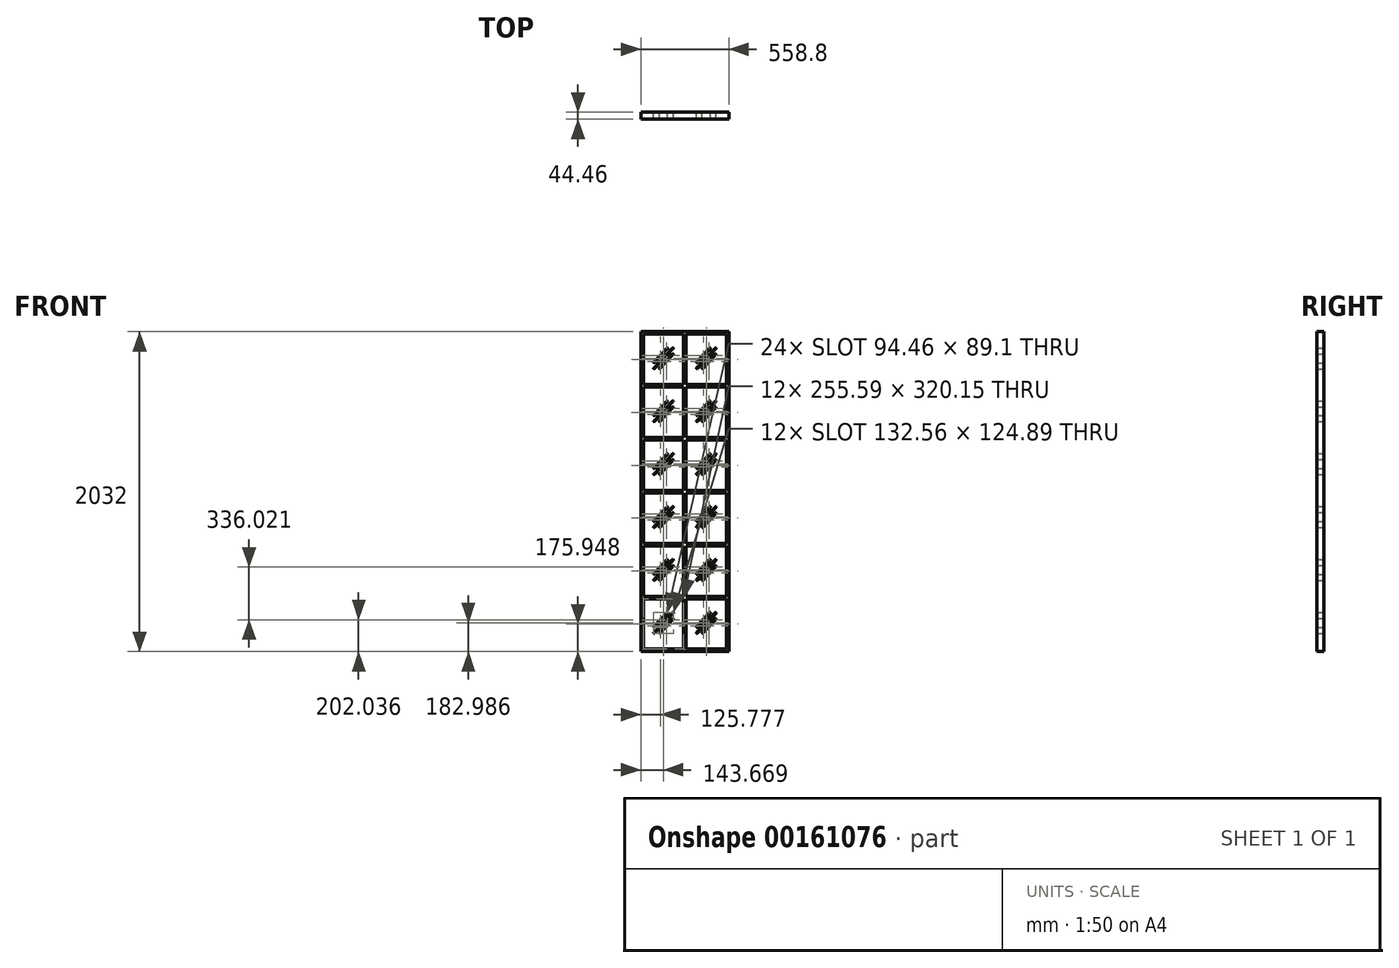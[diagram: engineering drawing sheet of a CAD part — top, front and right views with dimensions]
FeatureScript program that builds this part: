
annotation { "Feature Type Name" : "Feature", "Feature Type Description" : "" }
export const myFeature = defineFeature(function(context is Context, id is Id, definition is map)
    precondition{}
    {
        {
            var Q0;
            Q0=qCreatedBy(makeId("Front.planeOp"),FACE);
            var sketch = newSketch(context, id + "F0", { "sketchPlane" : qUnion([Q0])});
            skLineSegment(sketch, "E0.bottom", {"start": v(0, 0) * mm, "end": v(558.8, 0) * mm});
            skLineSegment(sketch, "E0.top", {"start": v(0, 2032) * mm, "end": v(558.8, 2032) * mm});
            skLineSegment(sketch, "E0.left", {"start": v(0, 0) * mm, "end": v(0, 2032) * mm});
            skLineSegment(sketch, "E0.right", {"start": v(558.8, 0) * mm, "end": v(558.8, 2032) * mm});
            skLineSegment(sketch, "E1.bottom", {"start": v(15.88, 15.88) * mm, "end": v(271.46, 15.88) * mm});
            skLineSegment(sketch, "E1.top", {"start": v(15.88, 336.02) * mm, "end": v(271.46, 336.02) * mm});
            skLineSegment(sketch, "E1.left", {"start": v(15.88, 15.88) * mm, "end": v(15.88, 336.02) * mm});
            skLineSegment(sketch, "E1.right", {"start": v(271.46, 15.88) * mm, "end": v(271.46, 336.02) * mm});
            skLineSegment(sketch, "E2.bottom", {"start": v(287.34, 15.88) * mm, "end": v(542.93, 15.88) * mm});
            skLineSegment(sketch, "E2.top", {"start": v(287.34, 336.02) * mm, "end": v(542.93, 336.02) * mm});
            skLineSegment(sketch, "E2.left", {"start": v(287.34, 15.88) * mm, "end": v(287.34, 336.02) * mm});
            skLineSegment(sketch, "E2.right", {"start": v(542.93, 15.88) * mm, "end": v(542.93, 336.02) * mm});
            skLineSegment(sketch, "E3.bottom", {"start": v(271.46, 351.9) * mm, "end": v(15.88, 351.9) * mm});
            skLineSegment(sketch, "E3.top", {"start": v(271.46, 672.04) * mm, "end": v(15.88, 672.04) * mm});
            skLineSegment(sketch, "E3.left", {"start": v(271.46, 351.9) * mm, "end": v(271.46, 672.04) * mm});
            skLineSegment(sketch, "E3.right", {"start": v(15.88, 351.9) * mm, "end": v(15.88, 672.04) * mm});
            skLineSegment(sketch, "E4.bottom", {"start": v(287.34, 351.9) * mm, "end": v(542.93, 351.9) * mm});
            skLineSegment(sketch, "E4.top", {"start": v(287.34, 672.04) * mm, "end": v(542.93, 672.04) * mm});
            skLineSegment(sketch, "E4.left", {"start": v(287.34, 351.9) * mm, "end": v(287.34, 672.04) * mm});
            skLineSegment(sketch, "E4.right", {"start": v(542.93, 351.9) * mm, "end": v(542.93, 672.04) * mm});
            skLineSegment(sketch, "E5.bottom", {"start": v(271.46, 687.92) * mm, "end": v(15.88, 687.92) * mm});
            skLineSegment(sketch, "E5.top", {"start": v(271.46, 1008.06) * mm, "end": v(15.88, 1008.06) * mm});
            skLineSegment(sketch, "E5.left", {"start": v(271.46, 687.92) * mm, "end": v(271.46, 1008.06) * mm});
            skLineSegment(sketch, "E5.right", {"start": v(15.88, 687.92) * mm, "end": v(15.87, 1008.06) * mm});
            skLineSegment(sketch, "E6.bottom", {"start": v(287.34, 687.92) * mm, "end": v(542.93, 687.92) * mm});
            skLineSegment(sketch, "E6.top", {"start": v(287.34, 1008.06) * mm, "end": v(542.93, 1008.06) * mm});
            skLineSegment(sketch, "E6.left", {"start": v(287.34, 687.92) * mm, "end": v(287.34, 1008.06) * mm});
            skLineSegment(sketch, "E6.right", {"start": v(542.93, 687.92) * mm, "end": v(542.93, 1008.06) * mm});
            skLineSegment(sketch, "E7.bottom", {"start": v(271.46, 1023.94) * mm, "end": v(15.88, 1023.94) * mm});
            skLineSegment(sketch, "E7.top", {"start": v(271.46, 1344.08) * mm, "end": v(15.87, 1344.08) * mm});
            skLineSegment(sketch, "E7.left", {"start": v(271.46, 1023.94) * mm, "end": v(271.46, 1344.08) * mm});
            skLineSegment(sketch, "E7.right", {"start": v(15.88, 1023.94) * mm, "end": v(15.87, 1344.08) * mm});
            skLineSegment(sketch, "E8.bottom", {"start": v(287.34, 1023.94) * mm, "end": v(542.93, 1023.94) * mm});
            skLineSegment(sketch, "E8.top", {"start": v(287.34, 1344.08) * mm, "end": v(542.93, 1344.08) * mm});
            skLineSegment(sketch, "E8.left", {"start": v(287.34, 1023.94) * mm, "end": v(287.34, 1344.08) * mm});
            skLineSegment(sketch, "E8.right", {"start": v(542.93, 1023.94) * mm, "end": v(542.93, 1344.08) * mm});
            skLineSegment(sketch, "E9.bottom", {"start": v(271.46, 1359.96) * mm, "end": v(15.87, 1359.96) * mm});
            skLineSegment(sketch, "E9.top", {"start": v(271.46, 1680.1) * mm, "end": v(15.87, 1680.1) * mm});
            skLineSegment(sketch, "E9.left", {"start": v(271.46, 1359.96) * mm, "end": v(271.46, 1680.1) * mm});
            skLineSegment(sketch, "E9.right", {"start": v(15.87, 1359.96) * mm, "end": v(15.87, 1680.1) * mm});
            skLineSegment(sketch, "E10.bottom", {"start": v(287.34, 1359.96) * mm, "end": v(542.93, 1359.96) * mm});
            skLineSegment(sketch, "E10.top", {"start": v(287.34, 1680.1) * mm, "end": v(542.93, 1680.1) * mm});
            skLineSegment(sketch, "E10.left", {"start": v(287.34, 1359.96) * mm, "end": v(287.34, 1680.1) * mm});
            skLineSegment(sketch, "E10.right", {"start": v(542.93, 1359.96) * mm, "end": v(542.93, 1680.1) * mm});
            skLineSegment(sketch, "E11.bottom", {"start": v(271.46, 1695.98) * mm, "end": v(15.87, 1695.98) * mm});
            skLineSegment(sketch, "E11.top", {"start": v(271.46, 2016.13) * mm, "end": v(15.87, 2016.13) * mm});
            skLineSegment(sketch, "E11.left", {"start": v(271.46, 1695.98) * mm, "end": v(271.46, 2016.13) * mm});
            skLineSegment(sketch, "E11.right", {"start": v(15.87, 1695.98) * mm, "end": v(15.87, 2016.13) * mm});
            skLineSegment(sketch, "E12.bottom", {"start": v(287.34, 1695.98) * mm, "end": v(542.93, 1695.98) * mm});
            skLineSegment(sketch, "E12.top", {"start": v(287.34, 2016.13) * mm, "end": v(542.93, 2016.13) * mm});
            skLineSegment(sketch, "E12.left", {"start": v(287.34, 1695.98) * mm, "end": v(287.34, 2016.13) * mm});
            skLineSegment(sketch, "E12.right", {"start": v(542.93, 1695.98) * mm, "end": v(542.93, 2016.13) * mm});
            skSolve(sketch);
        }
        {
            var Q0;
            Q0=qSketchRegion(id+"F0",true);
            extrude(context, id + "F1", {"entities" : qUnion([Q0]), "depth" : 22.22 * mm, "hasSecondDirection" : true, "secondDirectionOppositeDirection" : true, "secondDirectionDepth" : 22.22 * mm});
        }
        {
            var Q0;
            Q0=qCreatedBy(makeId("Front.planeOp"),FACE);
            var sketch = newSketch(context, id + "F2", { "sketchPlane" : qUnion([Q0])});
            skLineSegment(sketch, "E13.0", {"start": v(271.46, 1680.1) * mm, "end": v(15.87, 1680.1) * mm});
            skLineSegment(sketch, "E14.0", {"start": v(15.87, 1359.96) * mm, "end": v(15.87, 1680.1) * mm});
            skLineSegment(sketch, "E15.0", {"start": v(271.46, 1359.96) * mm, "end": v(15.87, 1359.96) * mm});
            skLineSegment(sketch, "E16.0", {"start": v(287.34, 1359.96) * mm, "end": v(542.93, 1359.96) * mm});
            skLineSegment(sketch, "E17.0", {"start": v(287.34, 1359.96) * mm, "end": v(287.34, 1680.1) * mm});
            skLineSegment(sketch, "E18.0", {"start": v(287.34, 1680.1) * mm, "end": v(542.93, 1680.1) * mm});
            skLineSegment(sketch, "E19.0", {"start": v(542.93, 1359.96) * mm, "end": v(542.93, 1680.1) * mm});
            skLineSegment(sketch, "E20.0", {"start": v(287.34, 1344.08) * mm, "end": v(542.93, 1344.08) * mm});
            skLineSegment(sketch, "E21.0", {"start": v(542.93, 1023.94) * mm, "end": v(542.93, 1344.08) * mm});
            skLineSegment(sketch, "E22.0", {"start": v(271.46, 1359.96) * mm, "end": v(271.46, 1680.1) * mm});
            skLineSegment(sketch, "E23.0", {"start": v(271.46, 1023.94) * mm, "end": v(271.46, 1344.08) * mm});
            skLineSegment(sketch, "E24.0", {"start": v(287.34, 1023.94) * mm, "end": v(542.93, 1023.94) * mm});
            skLineSegment(sketch, "E25.0", {"start": v(287.34, 1023.94) * mm, "end": v(287.34, 1344.08) * mm});
            skLineSegment(sketch, "E26.0", {"start": v(271.46, 1344.08) * mm, "end": v(15.87, 1344.08) * mm});
            skLineSegment(sketch, "E27.0", {"start": v(15.88, 1023.94) * mm, "end": v(15.87, 1344.08) * mm});
            skLineSegment(sketch, "E28.0", {"start": v(271.46, 1023.94) * mm, "end": v(15.88, 1023.94) * mm});
            skLineSegment(sketch, "E29.0", {"start": v(271.46, 1008.06) * mm, "end": v(15.88, 1008.06) * mm});
            skLineSegment(sketch, "E30.0", {"start": v(15.88, 687.92) * mm, "end": v(15.87, 1008.06) * mm});
            skLineSegment(sketch, "E31.0", {"start": v(271.46, 687.92) * mm, "end": v(271.46, 1008.06) * mm});
            skLineSegment(sketch, "E32.0", {"start": v(271.46, 687.92) * mm, "end": v(15.88, 687.92) * mm});
            skLineSegment(sketch, "E33.0", {"start": v(287.34, 687.92) * mm, "end": v(287.34, 1008.06) * mm});
            skLineSegment(sketch, "E34.0", {"start": v(287.34, 687.92) * mm, "end": v(542.93, 687.92) * mm});
            skLineSegment(sketch, "E35.0", {"start": v(542.93, 687.92) * mm, "end": v(542.93, 1008.06) * mm});
            skLineSegment(sketch, "E36.0", {"start": v(287.34, 1008.06) * mm, "end": v(542.93, 1008.06) * mm});
            skLineSegment(sketch, "E37.0", {"start": v(287.34, 672.04) * mm, "end": v(542.93, 672.04) * mm});
            skLineSegment(sketch, "E38.0", {"start": v(542.93, 351.9) * mm, "end": v(542.93, 672.04) * mm});
            skLineSegment(sketch, "E39.0", {"start": v(287.34, 351.9) * mm, "end": v(542.93, 351.9) * mm});
            skLineSegment(sketch, "E40.0", {"start": v(287.34, 351.9) * mm, "end": v(287.34, 672.04) * mm});
            skLineSegment(sketch, "E41.0", {"start": v(271.46, 351.9) * mm, "end": v(271.46, 672.04) * mm});
            skLineSegment(sketch, "E42.0", {"start": v(271.46, 351.9) * mm, "end": v(15.88, 351.9) * mm});
            skLineSegment(sketch, "E43.0", {"start": v(271.46, 672.04) * mm, "end": v(15.88, 672.04) * mm});
            skLineSegment(sketch, "E44.0", {"start": v(15.88, 351.9) * mm, "end": v(15.88, 672.04) * mm});
            skLineSegment(sketch, "E45.0", {"start": v(15.88, 336.02) * mm, "end": v(271.46, 336.02) * mm});
            skLineSegment(sketch, "E46.0", {"start": v(15.88, 15.88) * mm, "end": v(15.88, 336.02) * mm});
            skLineSegment(sketch, "E47.0", {"start": v(271.46, 15.88) * mm, "end": v(271.46, 336.02) * mm});
            skLineSegment(sketch, "E48.0", {"start": v(15.88, 15.88) * mm, "end": v(271.46, 15.88) * mm});
            skLineSegment(sketch, "E49.0", {"start": v(287.34, 15.88) * mm, "end": v(287.34, 336.02) * mm});
            skLineSegment(sketch, "E50.0", {"start": v(287.34, 15.88) * mm, "end": v(542.93, 15.88) * mm});
            skLineSegment(sketch, "E51.0", {"start": v(542.93, 15.88) * mm, "end": v(542.93, 336.02) * mm});
            skLineSegment(sketch, "E52.0", {"start": v(287.34, 336.02) * mm, "end": v(542.93, 336.02) * mm});
            skLineSegment(sketch, "E53", {"start": v(202.94, 246.1) * mm, "end": v(84.4, 119.88) * mm});
            skLineSegment(sketch, "E54", {"start": v(202.94, 208) * mm, "end": v(120.18, 119.88) * mm});
            skLineSegment(sketch, "E55", {"start": v(167.16, 246.1) * mm, "end": v(84.4, 157.98) * mm});
            skArc(sketch, "E56.0.startCap", {"start": v(164.84, 248.27) * mm, "mid": v(169.33, 248.4) * mm, "end": v(169.47, 243.92) * mm});
            skArc(sketch, "E56.0.endCap", {"start": v(86.71, 155.8) * mm, "mid": v(82.22, 155.67) * mm, "end": v(82.08, 160.15) * mm});
            skLineSegment(sketch, "E56.0.left", {"start": v(169.47, 243.92) * mm, "end": v(86.71, 155.8) * mm});
            skLineSegment(sketch, "E56.0.right", {"start": v(164.84, 248.27) * mm, "end": v(82.08, 160.15) * mm});
            skArc(sketch, "E56.1.startCap", {"start": v(200.63, 248.27) * mm, "mid": v(205.11, 248.4) * mm, "end": v(205.25, 243.92) * mm});
            skArc(sketch, "E56.1.endCap", {"start": v(86.71, 117.7) * mm, "mid": v(82.22, 117.57) * mm, "end": v(82.08, 122.05) * mm});
            skLineSegment(sketch, "E56.1.left", {"start": v(205.25, 243.92) * mm, "end": v(86.71, 117.7) * mm});
            skLineSegment(sketch, "E56.1.right", {"start": v(200.63, 248.27) * mm, "end": v(82.08, 122.05) * mm});
            skArc(sketch, "E56.2.startCap", {"start": v(200.63, 210.17) * mm, "mid": v(205.11, 210.3) * mm, "end": v(205.25, 205.82) * mm});
            skArc(sketch, "E56.2.endCap", {"start": v(122.5, 117.7) * mm, "mid": v(118, 117.57) * mm, "end": v(117.87, 122.05) * mm});
            skLineSegment(sketch, "E56.2.left", {"start": v(205.25, 205.82) * mm, "end": v(122.5, 117.7) * mm});
            skLineSegment(sketch, "E56.2.right", {"start": v(200.63, 210.17) * mm, "end": v(117.87, 122.05) * mm});
            skLineSegment(sketch, "E57.0.1.0", {"start": v(202.94, 582.11) * mm, "end": v(84.4, 455.9) * mm});
            skLineSegment(sketch, "E57.0.1.1", {"start": v(200.63, 546.19) * mm, "end": v(117.87, 458.07) * mm});
            skLineSegment(sketch, "E57.0.1.2", {"start": v(205.25, 579.94) * mm, "end": v(86.71, 453.73) * mm});
            skLineSegment(sketch, "E57.0.1.3", {"start": v(164.84, 584.29) * mm, "end": v(82.08, 496.17) * mm});
            skLineSegment(sketch, "E57.0.1.4", {"start": v(205.25, 541.84) * mm, "end": v(122.5, 453.73) * mm});
            skLineSegment(sketch, "E57.0.1.5", {"start": v(169.47, 579.94) * mm, "end": v(86.71, 491.83) * mm});
            skLineSegment(sketch, "E57.0.1.6", {"start": v(202.94, 544.01) * mm, "end": v(120.18, 455.9) * mm});
            skLineSegment(sketch, "E57.0.1.7", {"start": v(167.16, 582.11) * mm, "end": v(84.4, 494) * mm});
            skLineSegment(sketch, "E57.0.1.8", {"start": v(200.63, 584.29) * mm, "end": v(82.08, 458.07) * mm});
            skArc(sketch, "E57.0.1.9", {"start": v(164.84, 584.29) * mm, "mid": v(169.33, 584.43) * mm, "end": v(169.47, 579.94) * mm});
            skArc(sketch, "E57.0.1.10", {"start": v(200.63, 584.29) * mm, "mid": v(205.11, 584.43) * mm, "end": v(205.25, 579.94) * mm});
            skArc(sketch, "E57.0.1.11", {"start": v(86.71, 453.73) * mm, "mid": v(82.22, 453.59) * mm, "end": v(82.08, 458.07) * mm});
            skArc(sketch, "E57.0.1.12", {"start": v(86.71, 491.83) * mm, "mid": v(82.22, 491.69) * mm, "end": v(82.08, 496.17) * mm});
            skArc(sketch, "E57.0.1.13", {"start": v(122.5, 453.73) * mm, "mid": v(118, 453.59) * mm, "end": v(117.87, 458.07) * mm});
            skArc(sketch, "E57.0.1.14", {"start": v(200.63, 546.19) * mm, "mid": v(205.11, 546.33) * mm, "end": v(205.25, 541.84) * mm});
            skLineSegment(sketch, "E57.0.2.0", {"start": v(202.94, 918.13) * mm, "end": v(84.4, 791.92) * mm});
            skLineSegment(sketch, "E57.0.2.1", {"start": v(200.63, 882.2) * mm, "end": v(117.87, 794.1) * mm});
            skLineSegment(sketch, "E57.0.2.2", {"start": v(205.25, 915.96) * mm, "end": v(86.71, 789.75) * mm});
            skLineSegment(sketch, "E57.0.2.3", {"start": v(164.84, 920.3) * mm, "end": v(82.08, 832.2) * mm});
            skLineSegment(sketch, "E57.0.2.4", {"start": v(205.25, 877.86) * mm, "end": v(122.5, 789.75) * mm});
            skLineSegment(sketch, "E57.0.2.5", {"start": v(169.47, 915.96) * mm, "end": v(86.71, 827.85) * mm});
            skLineSegment(sketch, "E57.0.2.6", {"start": v(202.94, 880.03) * mm, "end": v(120.18, 791.92) * mm});
            skLineSegment(sketch, "E57.0.2.7", {"start": v(167.16, 918.13) * mm, "end": v(84.4, 830.02) * mm});
            skLineSegment(sketch, "E57.0.2.8", {"start": v(200.63, 920.3) * mm, "end": v(82.08, 794.1) * mm});
            skArc(sketch, "E57.0.2.9", {"start": v(164.84, 920.3) * mm, "mid": v(169.33, 920.45) * mm, "end": v(169.47, 915.96) * mm});
            skArc(sketch, "E57.0.2.10", {"start": v(200.63, 920.3) * mm, "mid": v(205.11, 920.45) * mm, "end": v(205.25, 915.96) * mm});
            skArc(sketch, "E57.0.2.11", {"start": v(86.71, 789.75) * mm, "mid": v(82.22, 789.6) * mm, "end": v(82.08, 794.1) * mm});
            skArc(sketch, "E57.0.2.12", {"start": v(86.71, 827.85) * mm, "mid": v(82.22, 827.7) * mm, "end": v(82.08, 832.2) * mm});
            skArc(sketch, "E57.0.2.13", {"start": v(122.5, 789.75) * mm, "mid": v(118, 789.6) * mm, "end": v(117.87, 794.1) * mm});
            skArc(sketch, "E57.0.2.14", {"start": v(200.63, 882.2) * mm, "mid": v(205.11, 882.35) * mm, "end": v(205.25, 877.86) * mm});
            skLineSegment(sketch, "E57.0.3.0", {"start": v(202.94, 1254.15) * mm, "end": v(84.4, 1127.94) * mm});
            skLineSegment(sketch, "E57.0.3.1", {"start": v(200.63, 1218.23) * mm, "end": v(117.87, 1130.12) * mm});
            skLineSegment(sketch, "E57.0.3.2", {"start": v(205.25, 1251.98) * mm, "end": v(86.71, 1125.77) * mm});
            skLineSegment(sketch, "E57.0.3.3", {"start": v(164.84, 1256.33) * mm, "end": v(82.08, 1168.22) * mm});
            skLineSegment(sketch, "E57.0.3.4", {"start": v(205.25, 1213.88) * mm, "end": v(122.5, 1125.77) * mm});
            skLineSegment(sketch, "E57.0.3.5", {"start": v(169.47, 1251.98) * mm, "end": v(86.71, 1163.87) * mm});
            skLineSegment(sketch, "E57.0.3.6", {"start": v(202.94, 1216.05) * mm, "end": v(120.18, 1127.94) * mm});
            skLineSegment(sketch, "E57.0.3.7", {"start": v(167.16, 1254.15) * mm, "end": v(84.4, 1166.04) * mm});
            skLineSegment(sketch, "E57.0.3.8", {"start": v(200.63, 1256.33) * mm, "end": v(82.08, 1130.12) * mm});
            skArc(sketch, "E57.0.3.9", {"start": v(164.84, 1256.33) * mm, "mid": v(169.33, 1256.47) * mm, "end": v(169.47, 1251.98) * mm});
            skArc(sketch, "E57.0.3.10", {"start": v(200.63, 1256.33) * mm, "mid": v(205.11, 1256.47) * mm, "end": v(205.25, 1251.98) * mm});
            skArc(sketch, "E57.0.3.11", {"start": v(86.71, 1125.77) * mm, "mid": v(82.22, 1125.63) * mm, "end": v(82.08, 1130.12) * mm});
            skArc(sketch, "E57.0.3.12", {"start": v(86.71, 1163.87) * mm, "mid": v(82.22, 1163.73) * mm, "end": v(82.08, 1168.22) * mm});
            skArc(sketch, "E57.0.3.13", {"start": v(122.5, 1125.77) * mm, "mid": v(118, 1125.63) * mm, "end": v(117.87, 1130.12) * mm});
            skArc(sketch, "E57.0.3.14", {"start": v(200.63, 1218.23) * mm, "mid": v(205.11, 1218.37) * mm, "end": v(205.25, 1213.88) * mm});
            skLineSegment(sketch, "E57.0.4.0", {"start": v(202.94, 1590.18) * mm, "end": v(84.4, 1463.96) * mm});
            skLineSegment(sketch, "E57.0.4.1", {"start": v(200.63, 1554.25) * mm, "end": v(117.87, 1466.14) * mm});
            skLineSegment(sketch, "E57.0.4.2", {"start": v(205.25, 1588) * mm, "end": v(86.71, 1461.79) * mm});
            skLineSegment(sketch, "E57.0.4.3", {"start": v(164.84, 1592.35) * mm, "end": v(82.08, 1504.24) * mm});
            skLineSegment(sketch, "E57.0.4.4", {"start": v(205.25, 1549.9) * mm, "end": v(122.5, 1461.79) * mm});
            skLineSegment(sketch, "E57.0.4.5", {"start": v(169.47, 1588) * mm, "end": v(86.71, 1499.89) * mm});
            skLineSegment(sketch, "E57.0.4.6", {"start": v(202.94, 1552.08) * mm, "end": v(120.18, 1463.96) * mm});
            skLineSegment(sketch, "E57.0.4.7", {"start": v(167.16, 1590.18) * mm, "end": v(84.4, 1502.06) * mm});
            skLineSegment(sketch, "E57.0.4.8", {"start": v(200.63, 1592.35) * mm, "end": v(82.08, 1466.14) * mm});
            skArc(sketch, "E57.0.4.9", {"start": v(164.84, 1592.35) * mm, "mid": v(169.33, 1592.49) * mm, "end": v(169.47, 1588) * mm});
            skArc(sketch, "E57.0.4.10", {"start": v(200.63, 1592.35) * mm, "mid": v(205.11, 1592.49) * mm, "end": v(205.25, 1588) * mm});
            skArc(sketch, "E57.0.4.11", {"start": v(86.71, 1461.79) * mm, "mid": v(82.22, 1461.65) * mm, "end": v(82.08, 1466.14) * mm});
            skArc(sketch, "E57.0.4.12", {"start": v(86.71, 1499.89) * mm, "mid": v(82.22, 1499.75) * mm, "end": v(82.08, 1504.24) * mm});
            skArc(sketch, "E57.0.4.13", {"start": v(122.5, 1461.79) * mm, "mid": v(118, 1461.65) * mm, "end": v(117.87, 1466.14) * mm});
            skArc(sketch, "E57.0.4.14", {"start": v(200.63, 1554.25) * mm, "mid": v(205.11, 1554.39) * mm, "end": v(205.25, 1549.9) * mm});
            skLineSegment(sketch, "E57.1.0.0", {"start": v(474.4, 246.1) * mm, "end": v(355.86, 119.88) * mm});
            skLineSegment(sketch, "E57.1.0.1", {"start": v(472.09, 210.17) * mm, "end": v(389.33, 122.05) * mm});
            skLineSegment(sketch, "E57.1.0.2", {"start": v(476.72, 243.92) * mm, "end": v(358.17, 117.7) * mm});
            skLineSegment(sketch, "E57.1.0.3", {"start": v(436.3, 248.27) * mm, "end": v(353.55, 160.15) * mm});
            skLineSegment(sketch, "E57.1.0.4", {"start": v(476.72, 205.82) * mm, "end": v(393.96, 117.7) * mm});
            skLineSegment(sketch, "E57.1.0.5", {"start": v(440.93, 243.92) * mm, "end": v(358.17, 155.8) * mm});
            skLineSegment(sketch, "E57.1.0.6", {"start": v(474.4, 208) * mm, "end": v(391.64, 119.88) * mm});
            skLineSegment(sketch, "E57.1.0.7", {"start": v(438.62, 246.1) * mm, "end": v(355.86, 157.98) * mm});
            skLineSegment(sketch, "E57.1.0.8", {"start": v(472.09, 248.27) * mm, "end": v(353.55, 122.05) * mm});
            skArc(sketch, "E57.1.0.9", {"start": v(436.3, 248.27) * mm, "mid": v(440.8, 248.4) * mm, "end": v(440.93, 243.92) * mm});
            skArc(sketch, "E57.1.0.10", {"start": v(472.09, 248.27) * mm, "mid": v(476.58, 248.4) * mm, "end": v(476.72, 243.92) * mm});
            skArc(sketch, "E57.1.0.11", {"start": v(358.17, 117.7) * mm, "mid": v(353.69, 117.57) * mm, "end": v(353.55, 122.05) * mm});
            skArc(sketch, "E57.1.0.12", {"start": v(358.17, 155.8) * mm, "mid": v(353.69, 155.67) * mm, "end": v(353.55, 160.15) * mm});
            skArc(sketch, "E57.1.0.13", {"start": v(393.96, 117.7) * mm, "mid": v(389.47, 117.57) * mm, "end": v(389.33, 122.05) * mm});
            skArc(sketch, "E57.1.0.14", {"start": v(472.09, 210.17) * mm, "mid": v(476.58, 210.3) * mm, "end": v(476.72, 205.82) * mm});
            skLineSegment(sketch, "E57.1.1.0", {"start": v(474.4, 582.11) * mm, "end": v(355.86, 455.9) * mm});
            skLineSegment(sketch, "E57.1.1.1", {"start": v(472.09, 546.19) * mm, "end": v(389.33, 458.07) * mm});
            skLineSegment(sketch, "E57.1.1.2", {"start": v(476.72, 579.94) * mm, "end": v(358.17, 453.73) * mm});
            skLineSegment(sketch, "E57.1.1.3", {"start": v(436.3, 584.29) * mm, "end": v(353.55, 496.17) * mm});
            skLineSegment(sketch, "E57.1.1.4", {"start": v(476.72, 541.84) * mm, "end": v(393.96, 453.73) * mm});
            skLineSegment(sketch, "E57.1.1.5", {"start": v(440.93, 579.94) * mm, "end": v(358.17, 491.83) * mm});
            skLineSegment(sketch, "E57.1.1.6", {"start": v(474.4, 544.01) * mm, "end": v(391.64, 455.9) * mm});
            skLineSegment(sketch, "E57.1.1.7", {"start": v(438.62, 582.11) * mm, "end": v(355.86, 494) * mm});
            skLineSegment(sketch, "E57.1.1.8", {"start": v(472.09, 584.29) * mm, "end": v(353.55, 458.07) * mm});
            skArc(sketch, "E57.1.1.9", {"start": v(436.3, 584.29) * mm, "mid": v(440.8, 584.43) * mm, "end": v(440.93, 579.94) * mm});
            skArc(sketch, "E57.1.1.10", {"start": v(472.09, 584.29) * mm, "mid": v(476.58, 584.43) * mm, "end": v(476.72, 579.94) * mm});
            skArc(sketch, "E57.1.1.11", {"start": v(358.17, 453.73) * mm, "mid": v(353.69, 453.59) * mm, "end": v(353.55, 458.07) * mm});
            skArc(sketch, "E57.1.1.12", {"start": v(358.17, 491.83) * mm, "mid": v(353.69, 491.69) * mm, "end": v(353.55, 496.17) * mm});
            skArc(sketch, "E57.1.1.13", {"start": v(393.96, 453.73) * mm, "mid": v(389.47, 453.59) * mm, "end": v(389.33, 458.07) * mm});
            skArc(sketch, "E57.1.1.14", {"start": v(472.09, 546.19) * mm, "mid": v(476.58, 546.33) * mm, "end": v(476.72, 541.84) * mm});
            skLineSegment(sketch, "E57.1.2.0", {"start": v(474.4, 918.13) * mm, "end": v(355.86, 791.92) * mm});
            skLineSegment(sketch, "E57.1.2.1", {"start": v(472.09, 882.2) * mm, "end": v(389.33, 794.1) * mm});
            skLineSegment(sketch, "E57.1.2.2", {"start": v(476.72, 915.96) * mm, "end": v(358.17, 789.75) * mm});
            skLineSegment(sketch, "E57.1.2.3", {"start": v(436.3, 920.3) * mm, "end": v(353.55, 832.2) * mm});
            skLineSegment(sketch, "E57.1.2.4", {"start": v(476.72, 877.86) * mm, "end": v(393.96, 789.75) * mm});
            skLineSegment(sketch, "E57.1.2.5", {"start": v(440.93, 915.96) * mm, "end": v(358.17, 827.85) * mm});
            skLineSegment(sketch, "E57.1.2.6", {"start": v(474.4, 880.03) * mm, "end": v(391.64, 791.92) * mm});
            skLineSegment(sketch, "E57.1.2.7", {"start": v(438.62, 918.13) * mm, "end": v(355.86, 830.02) * mm});
            skLineSegment(sketch, "E57.1.2.8", {"start": v(472.09, 920.3) * mm, "end": v(353.55, 794.1) * mm});
            skArc(sketch, "E57.1.2.9", {"start": v(436.3, 920.3) * mm, "mid": v(440.8, 920.45) * mm, "end": v(440.93, 915.96) * mm});
            skArc(sketch, "E57.1.2.10", {"start": v(472.09, 920.3) * mm, "mid": v(476.58, 920.45) * mm, "end": v(476.72, 915.96) * mm});
            skArc(sketch, "E57.1.2.11", {"start": v(358.17, 789.75) * mm, "mid": v(353.69, 789.6) * mm, "end": v(353.55, 794.1) * mm});
            skArc(sketch, "E57.1.2.12", {"start": v(358.17, 827.85) * mm, "mid": v(353.69, 827.7) * mm, "end": v(353.55, 832.2) * mm});
            skArc(sketch, "E57.1.2.13", {"start": v(393.96, 789.75) * mm, "mid": v(389.47, 789.6) * mm, "end": v(389.33, 794.1) * mm});
            skArc(sketch, "E57.1.2.14", {"start": v(472.09, 882.2) * mm, "mid": v(476.58, 882.35) * mm, "end": v(476.72, 877.86) * mm});
            skLineSegment(sketch, "E57.1.3.0", {"start": v(474.4, 1254.15) * mm, "end": v(355.86, 1127.94) * mm});
            skLineSegment(sketch, "E57.1.3.1", {"start": v(472.09, 1218.23) * mm, "end": v(389.33, 1130.12) * mm});
            skLineSegment(sketch, "E57.1.3.2", {"start": v(476.72, 1251.98) * mm, "end": v(358.17, 1125.77) * mm});
            skLineSegment(sketch, "E57.1.3.3", {"start": v(436.3, 1256.33) * mm, "end": v(353.55, 1168.22) * mm});
            skLineSegment(sketch, "E57.1.3.4", {"start": v(476.72, 1213.88) * mm, "end": v(393.96, 1125.77) * mm});
            skLineSegment(sketch, "E57.1.3.5", {"start": v(440.93, 1251.98) * mm, "end": v(358.17, 1163.87) * mm});
            skLineSegment(sketch, "E57.1.3.6", {"start": v(474.4, 1216.05) * mm, "end": v(391.64, 1127.94) * mm});
            skLineSegment(sketch, "E57.1.3.7", {"start": v(438.62, 1254.15) * mm, "end": v(355.86, 1166.04) * mm});
            skLineSegment(sketch, "E57.1.3.8", {"start": v(472.09, 1256.33) * mm, "end": v(353.55, 1130.12) * mm});
            skArc(sketch, "E57.1.3.9", {"start": v(436.3, 1256.33) * mm, "mid": v(440.8, 1256.47) * mm, "end": v(440.93, 1251.98) * mm});
            skArc(sketch, "E57.1.3.10", {"start": v(472.09, 1256.33) * mm, "mid": v(476.58, 1256.47) * mm, "end": v(476.72, 1251.98) * mm});
            skArc(sketch, "E57.1.3.11", {"start": v(358.17, 1125.77) * mm, "mid": v(353.69, 1125.63) * mm, "end": v(353.55, 1130.12) * mm});
            skArc(sketch, "E57.1.3.12", {"start": v(358.17, 1163.87) * mm, "mid": v(353.69, 1163.73) * mm, "end": v(353.55, 1168.22) * mm});
            skArc(sketch, "E57.1.3.13", {"start": v(393.96, 1125.77) * mm, "mid": v(389.47, 1125.63) * mm, "end": v(389.33, 1130.12) * mm});
            skArc(sketch, "E57.1.3.14", {"start": v(472.09, 1218.23) * mm, "mid": v(476.58, 1218.37) * mm, "end": v(476.72, 1213.88) * mm});
            skLineSegment(sketch, "E57.1.4.0", {"start": v(474.4, 1590.18) * mm, "end": v(355.86, 1463.96) * mm});
            skLineSegment(sketch, "E57.1.4.1", {"start": v(472.09, 1554.25) * mm, "end": v(389.33, 1466.14) * mm});
            skLineSegment(sketch, "E57.1.4.2", {"start": v(476.72, 1588) * mm, "end": v(358.17, 1461.79) * mm});
            skLineSegment(sketch, "E57.1.4.3", {"start": v(436.3, 1592.35) * mm, "end": v(353.55, 1504.24) * mm});
            skLineSegment(sketch, "E57.1.4.4", {"start": v(476.72, 1549.9) * mm, "end": v(393.96, 1461.79) * mm});
            skLineSegment(sketch, "E57.1.4.5", {"start": v(440.93, 1588) * mm, "end": v(358.17, 1499.89) * mm});
            skLineSegment(sketch, "E57.1.4.6", {"start": v(474.4, 1552.08) * mm, "end": v(391.64, 1463.96) * mm});
            skLineSegment(sketch, "E57.1.4.7", {"start": v(438.62, 1590.18) * mm, "end": v(355.86, 1502.06) * mm});
            skLineSegment(sketch, "E57.1.4.8", {"start": v(472.09, 1592.35) * mm, "end": v(353.55, 1466.14) * mm});
            skArc(sketch, "E57.1.4.9", {"start": v(436.3, 1592.35) * mm, "mid": v(440.8, 1592.49) * mm, "end": v(440.93, 1588) * mm});
            skArc(sketch, "E57.1.4.10", {"start": v(472.09, 1592.35) * mm, "mid": v(476.58, 1592.49) * mm, "end": v(476.72, 1588) * mm});
            skArc(sketch, "E57.1.4.11", {"start": v(358.17, 1461.79) * mm, "mid": v(353.69, 1461.65) * mm, "end": v(353.55, 1466.14) * mm});
            skArc(sketch, "E57.1.4.12", {"start": v(358.17, 1499.89) * mm, "mid": v(353.69, 1499.75) * mm, "end": v(353.55, 1504.24) * mm});
            skArc(sketch, "E57.1.4.13", {"start": v(393.96, 1461.79) * mm, "mid": v(389.47, 1461.65) * mm, "end": v(389.33, 1466.14) * mm});
            skArc(sketch, "E57.1.4.14", {"start": v(472.09, 1554.25) * mm, "mid": v(476.58, 1554.39) * mm, "end": v(476.72, 1549.9) * mm});
            skLineSegment(sketch, "E57.direction1", {"start": v(82.08, 122.05) * mm, "end": v(353.55, 122.05) * mm, "construction": true});
            skLineSegment(sketch, "E57.direction2", {"start": v(82.08, 122.05) * mm, "end": v(82.08, 458.07) * mm, "construction": true});
            skLineSegment(sketch, "E58.0", {"start": v(271.46, 2016.13) * mm, "end": v(15.87, 2016.13) * mm});
            skLineSegment(sketch, "E59.0", {"start": v(15.87, 1695.98) * mm, "end": v(15.87, 2016.13) * mm});
            skLineSegment(sketch, "E60.0", {"start": v(271.46, 1695.98) * mm, "end": v(15.87, 1695.98) * mm});
            skLineSegment(sketch, "E61.0", {"start": v(271.46, 1695.98) * mm, "end": v(271.46, 2016.13) * mm});
            skLineSegment(sketch, "E62.0", {"start": v(287.34, 1695.98) * mm, "end": v(287.34, 2016.13) * mm});
            skLineSegment(sketch, "E63.0", {"start": v(287.34, 1695.98) * mm, "end": v(542.93, 1695.98) * mm});
            skLineSegment(sketch, "E64.0", {"start": v(542.93, 1695.98) * mm, "end": v(542.93, 2016.13) * mm});
            skLineSegment(sketch, "E65.0", {"start": v(287.34, 2016.13) * mm, "end": v(542.93, 2016.13) * mm});
            skLineSegment(sketch, "E66.0.0.5", {"start": v(202.94, 1926.2) * mm, "end": v(84.4, 1799.98) * mm});
            skLineSegment(sketch, "E66.3.0.5", {"start": v(200.63, 1890.27) * mm, "end": v(117.87, 1802.16) * mm});
            skLineSegment(sketch, "E66.6.0.5", {"start": v(205.25, 1924.02) * mm, "end": v(86.71, 1797.81) * mm});
            skLineSegment(sketch, "E66.9.0.5", {"start": v(164.84, 1928.37) * mm, "end": v(82.08, 1840.26) * mm});
            skLineSegment(sketch, "E66.12.0.5", {"start": v(205.25, 1885.92) * mm, "end": v(122.5, 1797.81) * mm});
            skLineSegment(sketch, "E66.15.0.5", {"start": v(169.47, 1924.02) * mm, "end": v(86.71, 1835.91) * mm});
            skLineSegment(sketch, "E66.18.0.5", {"start": v(202.94, 1888.1) * mm, "end": v(120.18, 1799.98) * mm});
            skLineSegment(sketch, "E66.21.0.5", {"start": v(167.16, 1926.2) * mm, "end": v(84.4, 1838.08) * mm});
            skLineSegment(sketch, "E66.24.0.5", {"start": v(200.63, 1928.37) * mm, "end": v(82.08, 1802.16) * mm});
            skArc(sketch, "E66.27.0.5", {"start": v(164.84, 1928.37) * mm, "mid": v(169.33, 1928.51) * mm, "end": v(169.47, 1924.02) * mm});
            skArc(sketch, "E66.31.0.5", {"start": v(200.63, 1928.37) * mm, "mid": v(205.11, 1928.51) * mm, "end": v(205.25, 1924.02) * mm});
            skArc(sketch, "E66.35.0.5", {"start": v(86.71, 1797.81) * mm, "mid": v(82.22, 1797.67) * mm, "end": v(82.08, 1802.16) * mm});
            skArc(sketch, "E66.39.0.5", {"start": v(86.71, 1835.91) * mm, "mid": v(82.22, 1835.77) * mm, "end": v(82.08, 1840.26) * mm});
            skArc(sketch, "E66.43.0.5", {"start": v(122.5, 1797.81) * mm, "mid": v(118, 1797.67) * mm, "end": v(117.87, 1802.16) * mm});
            skArc(sketch, "E66.47.0.5", {"start": v(200.63, 1890.27) * mm, "mid": v(205.11, 1890.41) * mm, "end": v(205.25, 1885.92) * mm});
            skLineSegment(sketch, "E66.0.1.5", {"start": v(474.4, 1926.2) * mm, "end": v(355.86, 1799.98) * mm});
            skLineSegment(sketch, "E66.3.1.5", {"start": v(472.09, 1890.27) * mm, "end": v(389.33, 1802.16) * mm});
            skLineSegment(sketch, "E66.6.1.5", {"start": v(476.72, 1924.02) * mm, "end": v(358.17, 1797.81) * mm});
            skLineSegment(sketch, "E66.9.1.5", {"start": v(436.3, 1928.37) * mm, "end": v(353.55, 1840.26) * mm});
            skLineSegment(sketch, "E66.12.1.5", {"start": v(476.72, 1885.92) * mm, "end": v(393.96, 1797.81) * mm});
            skLineSegment(sketch, "E66.15.1.5", {"start": v(440.93, 1924.02) * mm, "end": v(358.17, 1835.91) * mm});
            skLineSegment(sketch, "E66.18.1.5", {"start": v(474.4, 1888.1) * mm, "end": v(391.64, 1799.98) * mm});
            skLineSegment(sketch, "E66.21.1.5", {"start": v(438.62, 1926.2) * mm, "end": v(355.86, 1838.08) * mm});
            skLineSegment(sketch, "E66.24.1.5", {"start": v(472.09, 1928.37) * mm, "end": v(353.55, 1802.16) * mm});
            skArc(sketch, "E66.27.1.5", {"start": v(436.3, 1928.37) * mm, "mid": v(440.8, 1928.51) * mm, "end": v(440.93, 1924.02) * mm});
            skArc(sketch, "E66.31.1.5", {"start": v(472.09, 1928.37) * mm, "mid": v(476.58, 1928.51) * mm, "end": v(476.72, 1924.02) * mm});
            skArc(sketch, "E66.35.1.5", {"start": v(358.17, 1797.81) * mm, "mid": v(353.69, 1797.67) * mm, "end": v(353.55, 1802.16) * mm});
            skArc(sketch, "E66.39.1.5", {"start": v(358.17, 1835.91) * mm, "mid": v(353.69, 1835.77) * mm, "end": v(353.55, 1840.26) * mm});
            skArc(sketch, "E66.43.1.5", {"start": v(393.96, 1797.81) * mm, "mid": v(389.47, 1797.67) * mm, "end": v(389.33, 1802.16) * mm});
            skArc(sketch, "E66.47.1.5", {"start": v(472.09, 1890.27) * mm, "mid": v(476.58, 1890.41) * mm, "end": v(476.72, 1885.92) * mm});
            skSolve(sketch);
        }
        {
            var Q0;
            Q0=qSketchRegion(id+"F2",true);
            extrude(context, id + "F3", {"entities" : qUnion([Q0]), "operationType" : NewBodyOperationType.ADD, "depth" : 21.59 * mm, "hasSecondDirection" : true, "secondDirectionOppositeDirection" : true, "secondDirectionDepth" : 21.59 * mm});
        }
    });
